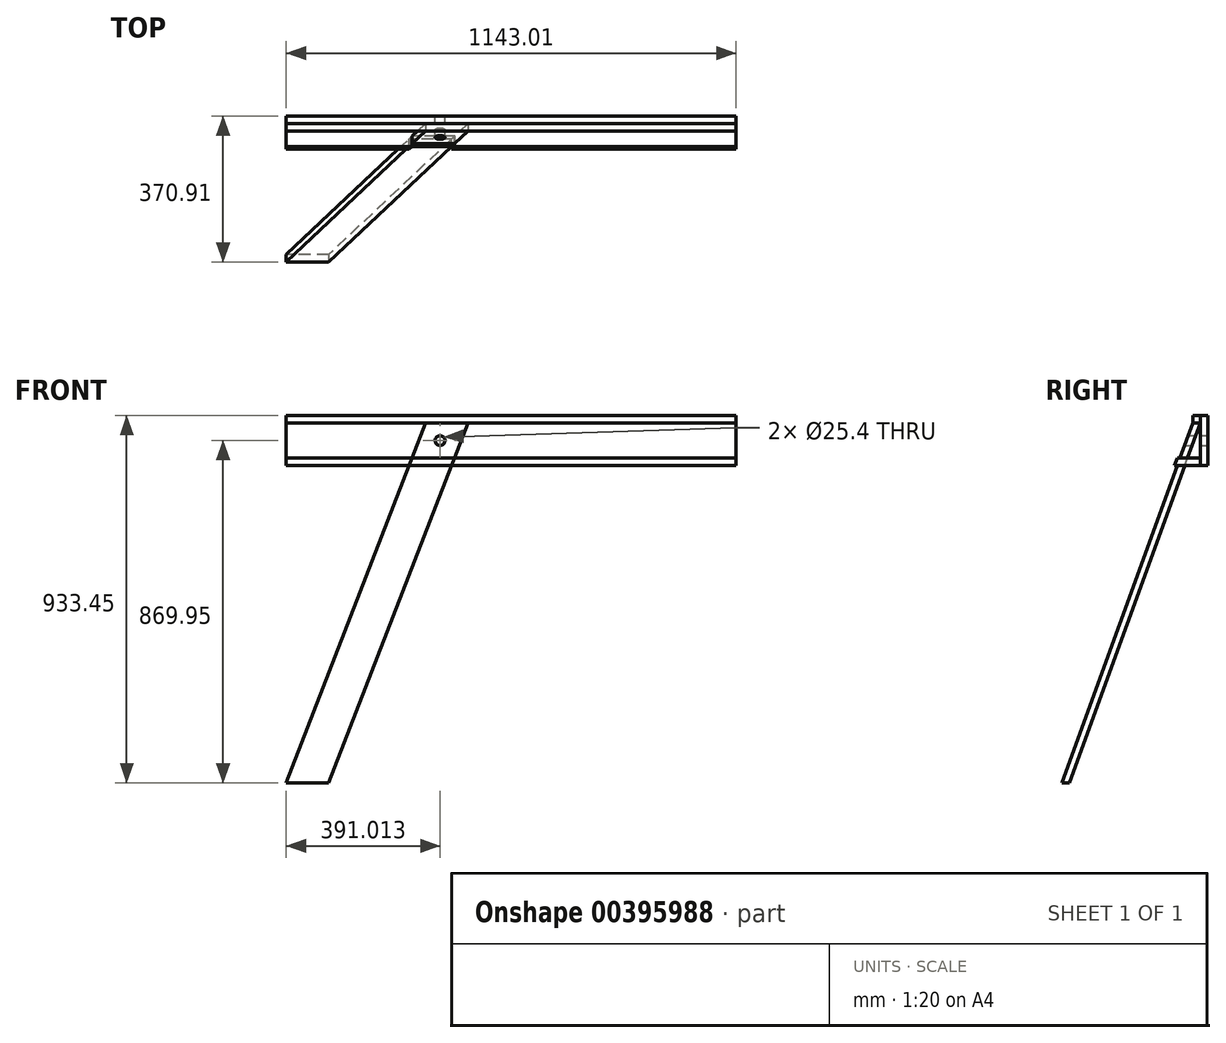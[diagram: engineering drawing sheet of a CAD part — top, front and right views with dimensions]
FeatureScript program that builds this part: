
annotation { "Feature Type Name" : "Feature", "Feature Type Description" : "" }
export const myFeature = defineFeature(function(context is Context, id is Id, definition is map)
    precondition{}
    {
        {
            var Q0;
            Q0=qCreatedBy(makeId("Right.planeOp"),FACE);
            var sketch = newSketch(context, id + "F0", { "sketchPlane" : qUnion([Q0])});
            skLineSegment(sketch, "E0.bottom", {"start": v(0, 0) * mm, "end": v(19.05, 0) * mm});
            skLineSegment(sketch, "E0.top", {"start": v(0, 127) * mm, "end": v(19.05, 127) * mm});
            skLineSegment(sketch, "E0.left", {"start": v(0, 0) * mm, "end": v(0, 127) * mm});
            skLineSegment(sketch, "E0.right", {"start": v(19.05, 0) * mm, "end": v(19.05, 127) * mm});
            skSolve(sketch);
        }
        {
            var Q0;
            Q0=makeQuery(id+"F0.imprint","IMPRINT",FACE,{"disambiguationData":[TD([[makeQuery(id+"F0.imprint","IMPRINT",EDGE,{"derivedFrom":sQuery(id+"F0.wireOp",EDGE,"E0.bottom")}),1.0]])]});
            extrude(context, id + "F1", {"entities" : qUnion([Q0]), "depth" : 1143 * mm});
        }
        {
            var Q0;
            Q0=qCreatedBy(makeId("Right.planeOp"),FACE);
            var sketch = newSketch(context, id + "F2", { "sketchPlane" : qUnion([Q0])});
            skLineSegment(sketch, "E1.bottom", {"start": v(0, 0) * mm, "end": v(-65.1, 0) * mm, "construction": true});
            skLineSegment(sketch, "E1.top", {"start": v(0, 19.05) * mm, "end": v(-65.1, 19.05) * mm, "construction": true});
            skLineSegment(sketch, "E1.left", {"start": v(0, 0) * mm, "end": v(0, 19.05) * mm, "construction": true});
            skLineSegment(sketch, "E1.right", {"start": v(-65.1, 0) * mm, "end": v(-65.1, 19.05) * mm, "construction": true});
            skLineSegment(sketch, "E2.bottom", {"start": v(0, 127) * mm, "end": v(-19.05, 127) * mm});
            skLineSegment(sketch, "E2.top", {"start": v(0, 107.95) * mm, "end": v(-19.05, 107.95) * mm});
            skLineSegment(sketch, "E2.left", {"start": v(0, 127) * mm, "end": v(0, 107.95) * mm});
            skLineSegment(sketch, "E2.right", {"start": v(-19.05, 127) * mm, "end": v(-19.05, 107.95) * mm});
            skLineSegment(sketch, "E3", {"start": v(-58.34, 0) * mm, "end": v(-19.05, 107.95) * mm, "construction": true});
            skLineSegment(sketch, "E4.bottom", {"start": v(0, 0) * mm, "end": v(-65.1, 0) * mm});
            skLineSegment(sketch, "E4.top", {"start": v(0, 19.05) * mm, "end": v(-58.16, 19.05) * mm});
            skLineSegment(sketch, "E4.left", {"start": v(0, 0) * mm, "end": v(0, 19.05) * mm});
            skLineSegment(sketch, "E5", {"start": v(-65.1, 0) * mm, "end": v(-65.1, 0) * mm});
            skLineSegment(sketch, "E6", {"start": v(-58.16, 19.05) * mm, "end": v(-65.1, 0) * mm});
            skSolve(sketch);
        }
        {
            var Q0;
            Q0=makeQuery(id+"F2.imprint","IMPRINT",FACE,{"disambiguationData":[TD([[makeQuery(id+"F2.imprint","IMPRINT",EDGE,{"derivedFrom":sQuery(id+"F2.wireOp",EDGE,"E2.bottom")}),1.0]])]});
            var Q1;
            Q1=makeQuery(id+"F1.opExtrude","CAP_FACE",FACE,{"disambiguationData":[OSD([sQuery(id+"F0.wireOp",EDGE,"E0.bottom"),sQuery(id+"F0.wireOp",EDGE,"E0.top"),sQuery(id+"F0.wireOp",EDGE,"E0.left"),sQuery(id+"F0.wireOp",EDGE,"E0.right")])],"isStart":false});
            extrude(context, id + "F3", {"entities" : qUnion([Q0]), "endBound" : BoundingType.UP_TO_SURFACE, "endBoundEntityFace" : qUnion([Q1]), "depth" : 25.4 * mm});
        }
        {
            var Q0;
            Q0=makeQuery(id+"F2.imprint","IMPRINT",FACE,{"disambiguationData":[TD([[makeQuery(id+"F2.imprint","IMPRINT",EDGE,{"derivedFrom":sQuery(id+"F2.wireOp",EDGE,"E4.bottom")}),-1.0]])]});
            var Q1;
            Q1=makeQuery(id+"F1.opExtrude","CAP_FACE",FACE,{"disambiguationData":[OSD([sQuery(id+"F0.wireOp",EDGE,"E0.bottom"),sQuery(id+"F0.wireOp",EDGE,"E0.top"),sQuery(id+"F0.wireOp",EDGE,"E0.left"),sQuery(id+"F0.wireOp",EDGE,"E0.right")])],"isStart":false});
            extrude(context, id + "F4", {"entities" : qUnion([Q0]), "endBound" : BoundingType.UP_TO_SURFACE, "endBoundEntityFace" : qUnion([Q1]), "depth" : 25.4 * mm});
        }
        {
            var Q0;
            Q0=makeQuery(id+"F1.opExtrude","SWEPT_FACE",FACE,{"disambiguationData":[OSD([sQuery(id+"F0.wireOp",EDGE,"E0.left")])]});
            var sketch = newSketch(context, id + "F5", { "sketchPlane" : qUnion([Q0])});
            skLineSegment(sketch, "E7", {"start": v(462.28, 107.95) * mm, "end": v(462.28, -806.45) * mm, "construction": true});
            skSolve(sketch);
        }
        {
            var Q0;
            Q0=sQuery(id+"F5.wireOp",EDGE,"E7");
            cPlane(context, id + "F6", {"entities" : qUnion([Q0]), "cplaneType" : CPlaneType.LINE_ANGLE, "offset" : 25.4 * mm, "angle" : 0 * degree, "width" : 152.4 * mm, "height" : 152.4 * mm});
        }
        {
            var Q0;
            Q0=qCreatedBy(id+"F6.planeOp",FACE);
            var sketch = newSketch(context, id + "F7", { "sketchPlane" : qUnion([Q0])});
            skLineSegment(sketch, "E8", {"start": v(0, 107.95) * mm, "end": v(332.81, -806.45) * mm, "construction": true});
            skLineSegment(sketch, "E9", {"start": v(332.81, -806.45) * mm, "end": v(0, -806.45) * mm, "construction": true});
            skSolve(sketch);
        }
        {
            var Q0;
            Q0=sQuery(id+"F7.wireOp",EDGE,"E8");
            cPlane(context, id + "F8", {"entities" : qUnion([Q0]), "cplaneType" : CPlaneType.LINE_ANGLE, "offset" : 25.4 * mm, "angle" : 90 * degree, "width" : 152.4 * mm, "height" : 152.4 * mm});
        }
        {
            var Q0;
            Q0=qCreatedBy(id+"F8.planeOp",FACE);
            var sketch = newSketch(context, id + "F9", { "sketchPlane" : qUnion([Q0])});
            skLineSegment(sketch, "E10", {"start": v(-462.28, 101.44) * mm, "end": v(-108.1, -871.64) * mm});
            skLineSegment(sketch, "E11", {"start": v(-108.1, -871.64) * mm, "end": v(0.01, -871.64) * mm});
            skLineSegment(sketch, "E12", {"start": v(0.01, -871.64) * mm, "end": v(-354.16, 101.44) * mm});
            skLineSegment(sketch, "E13", {"start": v(-354.16, 101.44) * mm, "end": v(-462.28, 101.44) * mm});
            skLineSegment(sketch, "E14", {"start": v(-108.1, -871.64) * mm, "end": v(-462.28, -871.64) * mm, "construction": true});
            skSolve(sketch);
        }
        {
            var Q0;
            Q0=makeQuery(id+"F9.imprint","IMPRINT",FACE,{"disambiguationData":[TD([[makeQuery(id+"F9.imprint","IMPRINT",EDGE,{"derivedFrom":sQuery(id+"F9.wireOp",EDGE,"E10")}),1.0]])]});
            var Q1;
            Q1=sQuery(id+"F2.wireOp",EDGE,"E2.top");
            sweep(context, id + "F10", {"profiles" : qUnion([Q0]), "path" : qUnion([Q1])});
        }
        {
            var Q0;
            Q0=makeQuery(id+"F4.opExtrude","SWEPT_FACE",FACE,{"disambiguationData":[OSD([sQuery(id+"F2.wireOp",EDGE,"E4.top")])]});
            var sketch = newSketch(context, id + "F11", { "sketchPlane" : qUnion([Q0])});
            skLineSegment(sketch, "E15", {"start": v(319.73, -58.16) * mm, "end": v(319.73, -32.36) * mm});
            skLineSegment(sketch, "E16", {"start": v(427.85, -32.36) * mm, "end": v(427.85, -58.16) * mm});
            skSolve(sketch);
        }
        {
            var Q0;
            Q0=makeQuery(id+"F4.opExtrude","SWEPT_FACE",FACE,{"disambiguationData":[OSD([sQuery(id+"F2.wireOp",EDGE,"E6")])]});
            var sketch = newSketch(context, id + "F12", { "sketchPlane" : qUnion([Q0])});
            skLineSegment(sketch, "E17", {"start": v(312.13, -22.26) * mm, "end": v(319.5, -2) * mm});
            skLineSegment(sketch, "E18", {"start": v(420.68, -22.26) * mm, "end": v(428.06, -2) * mm});
            skLineSegment(sketch, "E19", {"start": v(319.5, -2) * mm, "end": v(319.73, -2) * mm, "construction": true});
            skLineSegment(sketch, "E20", {"start": v(427.85, -2) * mm, "end": v(428.06, -2) * mm, "construction": true});
            skSolve(sketch);
        }
        {
            var Q0;
            {var subQ0=sQuery(id+"F12.wireOp",EDGE,"E17");Q0=makeQuery(id+"F12.imprint","IMPRINT",FACE,{"disambiguationData":[TD([[makeQuery(id+"F12.imprint","IMPRINT",EDGE,{"derivedFrom":subQ0}),-1.0]])]});}
            var Q1;
            Q1=sQuery(id+"F11.wireOp",EDGE,"E15");
            sweep(context, id + "F13", {"operationType" : NewBodyOperationType.REMOVE, "profiles" : qUnion([Q0]), "path" : qUnion([Q1])});
        }
        {
            var Q0;
            Q0=makeQuery(id+"F10.opSweep","CAP_FACE",FACE,{"disambiguationData":[OSD([sQuery(id+"F2.wireOp",VERTEX,"E2.top.end"),sQuery(id+"F9.wireOp",EDGE,"E10"),sQuery(id+"F9.wireOp",EDGE,"E11"),sQuery(id+"F9.wireOp",EDGE,"E12"),sQuery(id+"F9.wireOp",EDGE,"E13")])],"isStart":false});
            var sketch = newSketch(context, id + "F14", { "sketchPlane" : qUnion([Q0])});
            skLineSegment(sketch, "E21", {"start": v(408.22, 94.92) * mm, "end": v(373.79, 0.32) * mm, "construction": true});
            skLineSegment(sketch, "E22", {"start": v(391, 47.62) * mm, "end": v(445.06, 47.62) * mm, "construction": true});
            skLineSegment(sketch, "E23", {"start": v(391, 47.62) * mm, "end": v(336.94, 47.62) * mm, "construction": true});
            skSolve(sketch);
        }
        {
            var Q0;
            Q0=makeQuery(id+"F1.opExtrude","SWEPT_FACE",FACE,{"disambiguationData":[OSD([sQuery(id+"F0.wireOp",EDGE,"E0.right")])]});
            var sketch = newSketch(context, id + "F15", { "sketchPlane" : qUnion([Q0])});
            skCircle(sketch, "E24", {"center": v(-391, 63.5) * mm, "radius": 12.7 * mm});
            skSolve(sketch);
        }
        {
            var Q0;
            Q0=makeQuery(id+"F15.imprint","IMPRINT",FACE,{"disambiguationData":[TD([[makeQuery(id+"F15.imprint","IMPRINT",EDGE,{"derivedFrom":sQuery(id+"F15.wireOp",EDGE,"E24")}),1.0]])]});
            var Q1;
            Q1=sQuery(id+"F15.wireOp",EDGE,"E24");
            var Q2;
            Q2=makeQuery(id+"F10.opSweep","CAP_FACE",FACE,{"disambiguationData":[OSD([sQuery(id+"F2.wireOp",VERTEX,"E2.top.end"),sQuery(id+"F9.wireOp",EDGE,"E10"),sQuery(id+"F9.wireOp",EDGE,"E11"),sQuery(id+"F9.wireOp",EDGE,"E12"),sQuery(id+"F9.wireOp",EDGE,"E13")])],"isStart":false});
            extrude(context, id + "F16", {"entities" : qUnion([Q0]), "operationType" : NewBodyOperationType.REMOVE, "surfaceEntities" : qUnion([Q1]), "endBound" : BoundingType.UP_TO_SURFACE, "oppositeDirection" : true, "endBoundEntityFace" : qUnion([Q2]), "depth" : 25.4 * mm});
        }
    });
